# Revit family: Faucet-Wall_Mounted-American_Standard-Yoke-8355_Series
name_source: partatom
category: Plumbing Fixtures
revit_build: Autodesk Revit 2018 (Build: 20170223_1515(x64)
units: mm (PartAtom-declared; Revit-internal decimal feet)

## family parameters
Cut with Voids When Loaded = No
Host = Face
OmniClass Number = 23.45.55.17
OmniClass Title = Mixing Faucets
Part Type = Normal
Room Calculation Point = No
Round Connector Dimension = Use Diameter
Shared = Yes

## types (2) — shared parameters
ADA Compliant = Yes
Assembly Code = D2020300
CW Connection = Yes
CWFU = 1.5
Cold Water Connection Diameter = 1/2"
Default Elevation = 36"
Description = Exposed Yoke Wall-Mount Utility Faucet With Bottom Fork Brace and Offset Shanks.
HW Connection = Yes
HWFU = 1.5
Height = 2 3/4"
Hot Water Connection Diameter = 1/2"
Installation Type = Wall Mounted
Length = 5 7/8"
Manufacturer = American Standard
Material = Metal-American_Standard-002-Polished_Chrome
Price = Prices may vary. Please consult Manufacturer Representative for most up-to-date price list.
Product Documentation Link = https://www.americanstandard-us.com
Product Page URL = https://www.americanstandard-us.com
Revised Date = 02/08/2017
Specification = Exposed Yoke Wall-Mount Utility Faucet with Vacuum Breaker Bottom fork brace. Cast brass spout with vacuum breaker. Ceramic disc valves. Integral supply stops. Offset shanks with integral check valves. Vandal-resistant Wrist Blade Handles. Bucket hook. 3/4" threaded hose end. 1/2" NPT female inlets. Adjustable centers-to-centers: 6"-10" (152 - 254 mm).
URL = http://www.americanstandard-us.com
Vent Connection = No
Waste Connection = No
Width = 2 3/4"
zero-valued in all types: WFU

## per-type parameters (varying)
| type | Vacuum Breaker |
| 8355.101.002 | No |
| 8355.110.002 | Yes |

note: column(s) folded — value = type name in every type: Model

## geometry (parser evidence)
native form markers: Sweep x2
no freeform markers — native parametric forms only
